# Revit family: Door_Sliding_Single_Tormax_TX9600-ICU-3Panel
name_source: partatom
category: Doors
units: mm (PartAtom-declared; Revit-internal decimal feet)

## family parameters
Always vertical = Yes
Classification Number = 23.30.10.17.11
Cut with Voids When Loaded = No
Host = Wall
Room Calculation Point = No
Shared = No

## types (1)
- Door_Sliding_Single_Tormax_TX9600-ICU-3Panel
    Air Infiltration = as Specified
    Analytic Construction = <None>
    Assembly Code = B2030110
    Available Options = as Specified
    Breakout Width = 9' - 7 3/4"
    Breakout_Full = Yes
    Breakout_Partial = No
    Center Rail Width = 0' - 1 3/4"
    Clear Door Opening Width = 3' - 0 1/4"
    Construction Details = http://www.arcat.com
    Define Thermal Properties by = Schematic Type
    Description = Tormax Manual Sliding ICU Door as Specified
    Door Threshold = 9600SS : Recessed Threshold
    Expected Lifespan (Years) = 0
    Fire Rating = as Specified
    Frame Thickness = 0' - 4 1/2"
    Function = Exterior
    Glazing Stop Width = 0' - 0 1/4"
    Green Building-LEED = http://www.arcat.com
    Heat Transfer Coefficient (U) = 0.1 BTU/(h·ft²·°F)
    Include Transom = No
    Keynote = 08463
    Maintenance Schedule (Months) = 0
    Manufacturer = TORMAX USA Inc.
    Manufacturer Fax = 210-494-5930
    Manufacturer Website = http://www.tormaxusa.com
    Maximum Size = Width and Height as Specified
    Miami Dade Conformance = as Specified
    Model = as Specified
    Operating Temperature Range = as Specified
    Panel A Width = 3' - 9 1/2"
    Panel B Width = 3' - 3 1/2"
    Panel Thickness = 0' - 1 3/4"
    Product Data = http://www.arcat.com
    R = 0.0000 (h·ft²·°F)/BTU
    RO Spacing_Sides = 0' - 0 1/4"
    RO Spacing_Top = 0' - 0 1/4"
    SHGC = 0
    Sales Information = http://www.tormaxusa.com
    Send Message = http://www.arcat.com
    Smoke Rated = No
    Solar Heat Gain Coefficient = 0
    Specification = http://www.arcat.com
    Standards Conformance = as Specified
    Structural Test Pressure = as Specified
    Thermal Resistance (R) = 0.0000 (h·ft²·°F)/BTU
    Thickness = 0' - 1 3/4"
    Trackless = No
    U = 0.1 BTU/(h·ft²·°F)
    URL = http://www.tormaxusa.com
    VLT = 0
    Visual Light Transmittance = 0
    Wall Closure = By host
    Warranty Duration (Years) = 0
    Water Penetration = as Specified
    Width = 10' - 6"

## geometry (parser evidence)
native form markers: Blend x2, Sweep x13
no freeform markers — native parametric forms only
